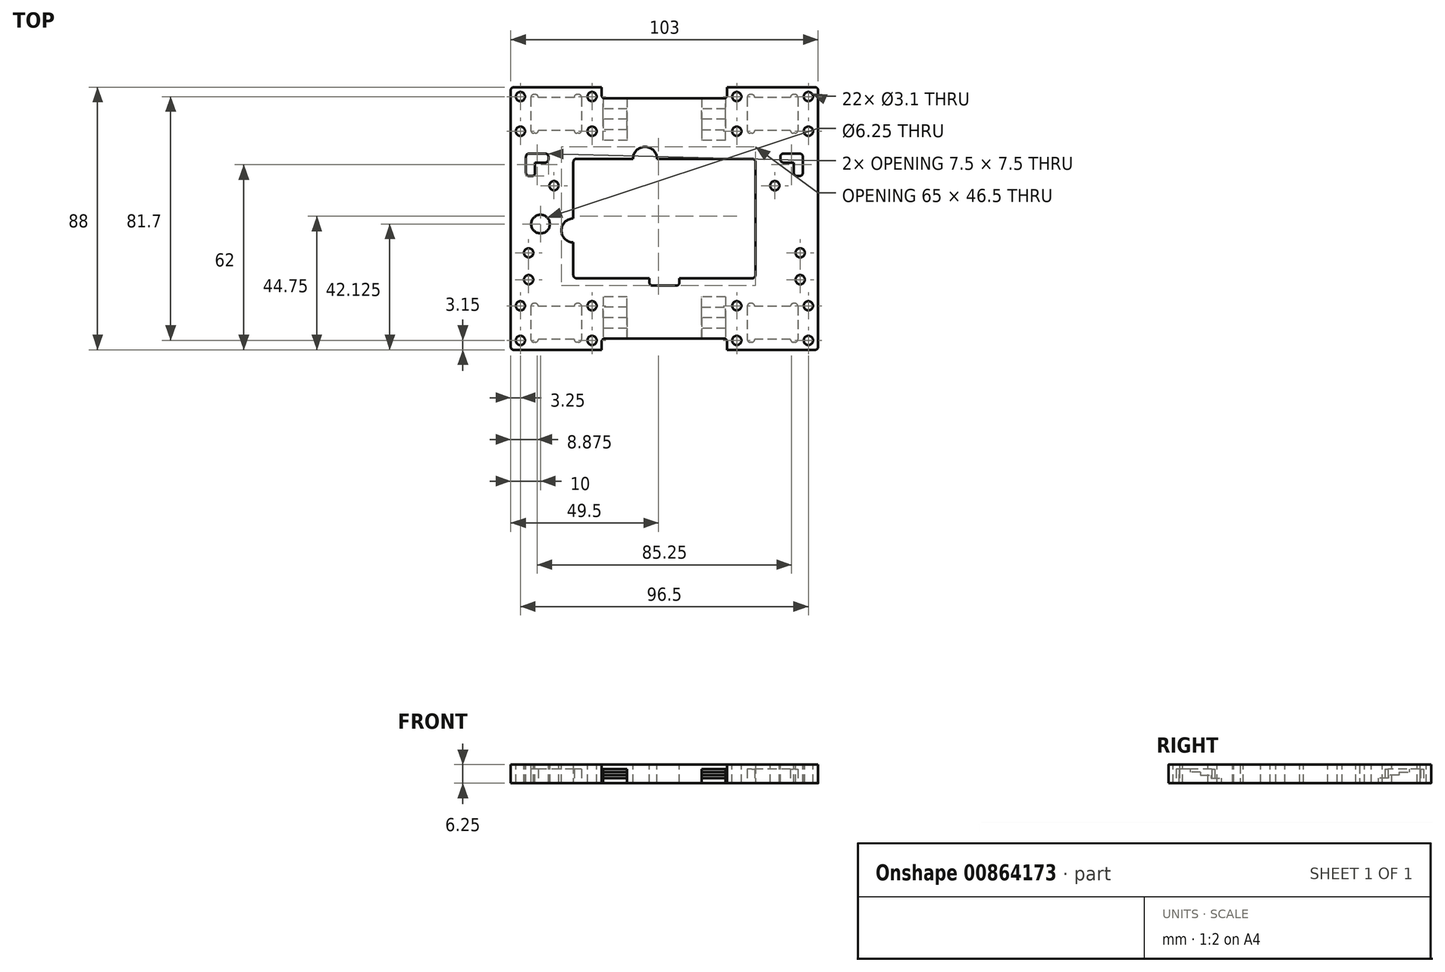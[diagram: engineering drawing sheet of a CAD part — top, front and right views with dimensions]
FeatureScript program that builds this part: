
annotation { "Feature Type Name" : "Feature", "Feature Type Description" : "" }
export const myFeature = defineFeature(function(context is Context, id is Id, definition is map)
    precondition{}
    {
        {
            var Q0;
            Q0=qCreatedBy(makeId("Top.planeOp"),FACE);
            var sketch = newSketch(context, id + "F0", { "sketchPlane" : qUnion([Q0])});
            skLineSegment(sketch, "E0.bottom", {"start": v(51.5, 44) * mm, "end": v(-51.5, 44) * mm, "construction": true});
            skLineSegment(sketch, "E0.top", {"start": v(51.5, -44) * mm, "end": v(-51.5, -44) * mm, "construction": true});
            skLineSegment(sketch, "E0.left", {"start": v(51.5, 44) * mm, "end": v(51.5, -44) * mm});
            skLineSegment(sketch, "E0.right", {"start": v(-51.5, 44) * mm, "end": v(-51.5, -44) * mm});
            skPoint(sketch, "E0.middle", {"position": v(0, 0) * mm});
            skLineSegment(sketch, "E1", {"start": v(-51.5, 44) * mm, "end": v(-21, 44) * mm, "construction": true});
            skLineSegment(sketch, "E2", {"start": v(-21, 44) * mm, "end": v(-21, 40.25) * mm});
            skLineSegment(sketch, "E3", {"start": v(-21, 40.25) * mm, "end": v(21, 40.25) * mm});
            skLineSegment(sketch, "E4", {"start": v(21, 40.25) * mm, "end": v(21, 44) * mm});
            skLineSegment(sketch, "E5", {"start": v(21, 44) * mm, "end": v(51.5, 44) * mm, "construction": true});
            skLineSegment(sketch, "E6", {"start": v(51.5, -44) * mm, "end": v(21, -44) * mm, "construction": true});
            skLineSegment(sketch, "E7", {"start": v(21, -44) * mm, "end": v(21, -40.25) * mm});
            skLineSegment(sketch, "E8", {"start": v(21, -40.25) * mm, "end": v(-21, -40.25) * mm});
            skLineSegment(sketch, "E9", {"start": v(-21, -40.25) * mm, "end": v(-21, -44) * mm});
            skLineSegment(sketch, "E10", {"start": v(-21, -44) * mm, "end": v(-51.5, -44) * mm, "construction": true});
            skLineSegment(sketch, "E11", {"start": v(0, 40.25) * mm, "end": v(0, 0) * mm, "construction": true});
            skLineSegment(sketch, "E12", {"start": v(0, -40.25) * mm, "end": v(0, 0) * mm, "construction": true});
            skLineSegment(sketch, "E13", {"start": v(-51.5, 44) * mm, "end": v(-21, 44) * mm});
            skLineSegment(sketch, "E14", {"start": v(21, 44) * mm, "end": v(51.5, 44) * mm});
            skLineSegment(sketch, "E15", {"start": v(51.5, -44) * mm, "end": v(21, -44) * mm});
            skLineSegment(sketch, "E16", {"start": v(-21, -44) * mm, "end": v(-51.5, -44) * mm});
            skLineSegment(sketch, "E17.bottom", {"start": v(30.5, 20) * mm, "end": v(-30.5, 20) * mm});
            skLineSegment(sketch, "E17.top", {"start": v(30.5, -20) * mm, "end": v(-30.5, -20) * mm});
            skLineSegment(sketch, "E17.left", {"start": v(30.5, 20) * mm, "end": v(30.5, -20) * mm});
            skLineSegment(sketch, "E17.right", {"start": v(-30.5, 20) * mm, "end": v(-30.5, -20) * mm});
            skSolve(sketch);
        }
        {
            var Q0;
            Q0=makeQuery(id+"F0.imprint","IMPRINT",FACE,{"disambiguationData":[TD([[makeQuery(id+"F0.imprint","IMPRINT",EDGE,{"derivedFrom":sQuery(id+"F0.wireOp",EDGE,"E0.left")}),-1.0]])]});
            extrude(context, id + "F1", {"entities" : qUnion([Q0]), "depth" : 6.25 * mm, "offsetDistance" : 25 * mm});
        }
        {
            var Q0;
            Q0=makeQuery(id+"F1.opExtrude","CAP_FACE",FACE,{"disambiguationData":[OSD([sQuery(id+"F0.wireOp",EDGE,"E0.left"),sQuery(id+"F0.wireOp",EDGE,"E0.right"),sQuery(id+"F0.wireOp",EDGE,"E2"),sQuery(id+"F0.wireOp",EDGE,"E3"),sQuery(id+"F0.wireOp",EDGE,"E4"),sQuery(id+"F0.wireOp",EDGE,"E7"),sQuery(id+"F0.wireOp",EDGE,"E8"),sQuery(id+"F0.wireOp",EDGE,"E9"),sQuery(id+"F0.wireOp",EDGE,"E13"),sQuery(id+"F0.wireOp",EDGE,"E14"),sQuery(id+"F0.wireOp",EDGE,"E15"),sQuery(id+"F0.wireOp",EDGE,"E16"),sQuery(id+"F0.wireOp",EDGE,"E17.bottom"),sQuery(id+"F0.wireOp",EDGE,"E17.top"),sQuery(id+"F0.wireOp",EDGE,"E17.left"),sQuery(id+"F0.wireOp",EDGE,"E17.right")])],"isStart":false});
            var sketch = newSketch(context, id + "F2", { "sketchPlane" : qUnion([Q0])});
            skLineSegment(sketch, "E18.bottom", {"start": v(-48.25, 40.85) * mm, "end": v(-24.25, 40.85) * mm, "construction": true});
            skLineSegment(sketch, "E18.top", {"start": v(-48.25, 29.25) * mm, "end": v(-24.25, 29.25) * mm, "construction": true});
            skLineSegment(sketch, "E18.left", {"start": v(-48.25, 40.85) * mm, "end": v(-48.25, 29.25) * mm, "construction": true});
            skLineSegment(sketch, "E18.right", {"start": v(-24.25, 40.85) * mm, "end": v(-24.25, 29.25) * mm, "construction": true});
            skLineSegment(sketch, "E19.bottom", {"start": v(24.25, 40.85) * mm, "end": v(48.25, 40.85) * mm, "construction": true});
            skLineSegment(sketch, "E19.top", {"start": v(24.25, 29.25) * mm, "end": v(48.25, 29.25) * mm, "construction": true});
            skLineSegment(sketch, "E19.left", {"start": v(24.25, 40.85) * mm, "end": v(24.25, 29.25) * mm, "construction": true});
            skLineSegment(sketch, "E19.right", {"start": v(48.25, 40.85) * mm, "end": v(48.25, 29.25) * mm, "construction": true});
            skLineSegment(sketch, "E20.bottom", {"start": v(24.25, -29.25) * mm, "end": v(48.25, -29.25) * mm, "construction": true});
            skLineSegment(sketch, "E20.top", {"start": v(24.25, -40.85) * mm, "end": v(48.25, -40.85) * mm, "construction": true});
            skLineSegment(sketch, "E20.left", {"start": v(24.25, -29.25) * mm, "end": v(24.25, -40.85) * mm, "construction": true});
            skLineSegment(sketch, "E20.right", {"start": v(48.25, -29.25) * mm, "end": v(48.25, -40.85) * mm, "construction": true});
            skLineSegment(sketch, "E21.bottom", {"start": v(-48.25, -29.25) * mm, "end": v(-24.25, -29.25) * mm, "construction": true});
            skLineSegment(sketch, "E21.top", {"start": v(-48.25, -40.85) * mm, "end": v(-24.25, -40.85) * mm, "construction": true});
            skLineSegment(sketch, "E21.left", {"start": v(-48.25, -29.25) * mm, "end": v(-48.25, -40.85) * mm, "construction": true});
            skLineSegment(sketch, "E21.right", {"start": v(-24.25, -29.25) * mm, "end": v(-24.25, -40.85) * mm, "construction": true});
            skLineSegment(sketch, "E22", {"start": v(-24.25, 29.25) * mm, "end": v(24.25, 29.25) * mm, "construction": true});
            skLineSegment(sketch, "E23", {"start": v(24.25, -29.25) * mm, "end": v(-24.25, -29.25) * mm, "construction": true});
            skLineSegment(sketch, "E24", {"start": v(0, 29.25) * mm, "end": v(0, 0) * mm, "construction": true});
            skLineSegment(sketch, "E25", {"start": v(0, 0) * mm, "end": v(0, -29.25) * mm, "construction": true});
            skCircle(sketch, "E26", {"center": v(-48.25, 40.85) * mm, "radius": 1.55 * mm});
            skCircle(sketch, "E27", {"center": v(-24.25, 40.85) * mm, "radius": 1.55 * mm});
            skCircle(sketch, "E28", {"center": v(-24.25, 29.25) * mm, "radius": 1.55 * mm});
            skCircle(sketch, "E29", {"center": v(-48.25, 29.25) * mm, "radius": 1.55 * mm});
            skCircle(sketch, "E30", {"center": v(24.25, 40.85) * mm, "radius": 1.55 * mm});
            skCircle(sketch, "E31", {"center": v(48.25, 40.85) * mm, "radius": 1.55 * mm});
            skCircle(sketch, "E32", {"center": v(48.25, 29.25) * mm, "radius": 1.55 * mm});
            skCircle(sketch, "E33", {"center": v(24.25, 29.25) * mm, "radius": 1.55 * mm});
            skCircle(sketch, "E34", {"center": v(24.25, -29.25) * mm, "radius": 1.55 * mm});
            skCircle(sketch, "E35", {"center": v(24.25, -40.85) * mm, "radius": 1.55 * mm});
            skCircle(sketch, "E36", {"center": v(48.25, -29.25) * mm, "radius": 1.55 * mm});
            skCircle(sketch, "E37", {"center": v(48.25, -40.85) * mm, "radius": 1.55 * mm});
            skCircle(sketch, "E38", {"center": v(-24.25, -29.25) * mm, "radius": 1.55 * mm});
            skCircle(sketch, "E39", {"center": v(-48.25, -29.25) * mm, "radius": 1.55 * mm});
            skCircle(sketch, "E40", {"center": v(-48.25, -40.85) * mm, "radius": 1.55 * mm});
            skCircle(sketch, "E41", {"center": v(-24.25, -40.85) * mm, "radius": 1.55 * mm});
            skLineSegment(sketch, "E42", {"start": v(-46.38, 21.75) * mm, "end": v(-38.88, 21.75) * mm});
            skLineSegment(sketch, "E43", {"start": v(-38.88, 21.75) * mm, "end": v(-38.88, 18.75) * mm});
            skLineSegment(sketch, "E44", {"start": v(-38.88, 18.75) * mm, "end": v(-43.38, 18.75) * mm});
            skLineSegment(sketch, "E45", {"start": v(-43.38, 18.75) * mm, "end": v(-43.38, 14.25) * mm});
            skLineSegment(sketch, "E46", {"start": v(-43.38, 14.25) * mm, "end": v(-46.38, 14.25) * mm});
            skLineSegment(sketch, "E47", {"start": v(-46.38, 14.25) * mm, "end": v(-46.38, 21.75) * mm});
            skLineSegment(sketch, "E48", {"start": v(38.88, 21.75) * mm, "end": v(46.38, 21.75) * mm});
            skLineSegment(sketch, "E49", {"start": v(46.38, 21.75) * mm, "end": v(46.38, 14.25) * mm});
            skLineSegment(sketch, "E50", {"start": v(46.38, 14.25) * mm, "end": v(43.38, 14.25) * mm});
            skLineSegment(sketch, "E51", {"start": v(43.38, 14.25) * mm, "end": v(43.38, 18.75) * mm});
            skLineSegment(sketch, "E52", {"start": v(43.38, 18.75) * mm, "end": v(38.88, 18.75) * mm});
            skLineSegment(sketch, "E53", {"start": v(38.88, 18.75) * mm, "end": v(38.88, 21.75) * mm});
            skLineSegment(sketch, "E54", {"start": v(-38.88, 21.75) * mm, "end": v(38.88, 21.75) * mm, "construction": true});
            skLineSegment(sketch, "E55", {"start": v(0, 21.75) * mm, "end": v(0, 0) * mm});
            skLineSegment(sketch, "E56", {"start": v(-37, 11) * mm, "end": v(37, 11) * mm, "construction": true});
            skLineSegment(sketch, "E57", {"start": v(0, 11) * mm, "end": v(0, 0) * mm});
            skCircle(sketch, "E58", {"center": v(-37, 11) * mm, "radius": 1.55 * mm});
            skCircle(sketch, "E59", {"center": v(37, 11) * mm, "radius": 1.55 * mm});
            skLineSegment(sketch, "E60.bottom", {"start": v(45.5, -11.5) * mm, "end": v(-45.5, -11.5) * mm, "construction": true});
            skLineSegment(sketch, "E60.top", {"start": v(45.5, -20.5) * mm, "end": v(-45.5, -20.5) * mm, "construction": true});
            skLineSegment(sketch, "E60.left", {"start": v(45.5, -11.5) * mm, "end": v(45.5, -20.5) * mm, "construction": true});
            skLineSegment(sketch, "E60.right", {"start": v(-45.5, -11.5) * mm, "end": v(-45.5, -20.5) * mm, "construction": true});
            skPoint(sketch, "E60.middle", {"position": v(0, -16) * mm});
            skCircle(sketch, "E61", {"center": v(-45.5, -11.5) * mm, "radius": 1.55 * mm});
            skCircle(sketch, "E62", {"center": v(-45.5, -20.5) * mm, "radius": 1.55 * mm});
            skCircle(sketch, "E63", {"center": v(45.5, -11.5) * mm, "radius": 1.55 * mm});
            skCircle(sketch, "E64", {"center": v(45.5, -20.5) * mm, "radius": 1.55 * mm});
            skCircle(sketch, "E65", {"center": v(-41.5, -1.87) * mm, "radius": 3.12 * mm});
            skSolve(sketch);
        }
        {
            var Q0;
            Q0 = qSketchRegion(id + "F2", true);
            extrude(context, id + "F3", {"entities" : qUnion([Q0]), "operationType" : NewBodyOperationType.REMOVE, "oppositeDirection" : true, "depth" : 25 * mm, "offsetDistance" : 25 * mm});
        }
        {
            var Q0;
            Q0=makeQuery(id+"F1.opExtrude","CAP_FACE",FACE,{"disambiguationData":[OSD([sQuery(id+"F0.wireOp",EDGE,"E0.left"),sQuery(id+"F0.wireOp",EDGE,"E0.right"),sQuery(id+"F0.wireOp",EDGE,"E2"),sQuery(id+"F0.wireOp",EDGE,"E3"),sQuery(id+"F0.wireOp",EDGE,"E4"),sQuery(id+"F0.wireOp",EDGE,"E7"),sQuery(id+"F0.wireOp",EDGE,"E8"),sQuery(id+"F0.wireOp",EDGE,"E9"),sQuery(id+"F0.wireOp",EDGE,"E13"),sQuery(id+"F0.wireOp",EDGE,"E14"),sQuery(id+"F0.wireOp",EDGE,"E15"),sQuery(id+"F0.wireOp",EDGE,"E16"),sQuery(id+"F0.wireOp",EDGE,"E17.bottom"),sQuery(id+"F0.wireOp",EDGE,"E17.top"),sQuery(id+"F0.wireOp",EDGE,"E17.left"),sQuery(id+"F0.wireOp",EDGE,"E17.right")])],"isStart":false});
            var sketch = newSketch(context, id + "F4", { "sketchPlane" : qUnion([Q0])});
            skCircle(sketch, "E66", {"center": v(-6.5, 20) * mm, "radius": 4 * mm});
            skCircle(sketch, "E67", {"center": v(-30.5, -4) * mm, "radius": 4 * mm});
            skLineSegment(sketch, "E68.bottom", {"start": v(-5, -20) * mm, "end": v(5, -20) * mm});
            skLineSegment(sketch, "E68.top", {"start": v(-5, -22.5) * mm, "end": v(5, -22.5) * mm});
            skLineSegment(sketch, "E68.left", {"start": v(-5, -20) * mm, "end": v(-5, -22.5) * mm});
            skLineSegment(sketch, "E68.right", {"start": v(5, -20) * mm, "end": v(5, -22.5) * mm});
            skLineSegment(sketch, "E69", {"start": v(0, 0) * mm, "end": v(0, -20) * mm, "construction": true});
            skSolve(sketch);
        }
        {
            var Q0;
            Q0 = qSketchRegion(id + "F4", true);
            extrude(context, id + "F5", {"entities" : qUnion([Q0]), "operationType" : NewBodyOperationType.REMOVE, "oppositeDirection" : true, "depth" : 25 * mm, "offsetDistance" : 25 * mm});
        }
        {
            var Q0;
            Q0=makeQuery(id+"F1.opExtrude","SWEPT_EDGE",EDGE,{"disambiguationData":[OSD([sQuery(id+"F0.wireOp",EDGE,"E0.left"),sQuery(id+"F0.wireOp",EDGE,"E14")])]});
            var Q1;
            Q1=makeQuery(id+"F1.opExtrude","SWEPT_EDGE",EDGE,{"disambiguationData":[OSD([sQuery(id+"F0.wireOp",EDGE,"E2"),sQuery(id+"F0.wireOp",EDGE,"E3")])]});
            var Q2;
            Q2=makeQuery(id+"F1.opExtrude","SWEPT_EDGE",EDGE,{"disambiguationData":[OSD([sQuery(id+"F0.wireOp",EDGE,"E3"),sQuery(id+"F0.wireOp",EDGE,"E4")])]});
            var Q3;
            Q3=makeQuery(id+"F1.opExtrude","SWEPT_EDGE",EDGE,{"disambiguationData":[OSD([sQuery(id+"F0.wireOp",EDGE,"E0.right"),sQuery(id+"F0.wireOp",EDGE,"E13")])]});
            var Q4;
            Q4=makeQuery(id+"F3.boolean.opBoolean","COPY",EDGE,{"derivedFrom":makeQuery(id+"F3.opExtrude","SWEPT_EDGE",EDGE,{"disambiguationData":[OSD([sQuery(id+"F2.wireOp",EDGE,"E49"),sQuery(id+"F2.wireOp",EDGE,"E50")])]})});
            var Q5;
            Q5=makeQuery(id+"F3.boolean.opBoolean","COPY",EDGE,{"derivedFrom":makeQuery(id+"F3.opExtrude","SWEPT_EDGE",EDGE,{"disambiguationData":[OSD([sQuery(id+"F2.wireOp",EDGE,"E50"),sQuery(id+"F2.wireOp",EDGE,"E51")])]})});
            var Q6;
            Q6=makeQuery(id+"F3.boolean.opBoolean","COPY",EDGE,{"derivedFrom":makeQuery(id+"F3.opExtrude","SWEPT_EDGE",EDGE,{"disambiguationData":[OSD([sQuery(id+"F2.wireOp",EDGE,"E52"),sQuery(id+"F2.wireOp",EDGE,"E53")])]})});
            var Q7;
            Q7=makeQuery(id+"F3.boolean.opBoolean","COPY",EDGE,{"derivedFrom":makeQuery(id+"F3.opExtrude","SWEPT_EDGE",EDGE,{"disambiguationData":[OSD([sQuery(id+"F2.wireOp",EDGE,"E48"),sQuery(id+"F2.wireOp",EDGE,"E53")])]})});
            var Q8;
            Q8=makeQuery(id+"F3.boolean.opBoolean","COPY",EDGE,{"derivedFrom":makeQuery(id+"F3.opExtrude","SWEPT_EDGE",EDGE,{"disambiguationData":[OSD([sQuery(id+"F2.wireOp",EDGE,"E48"),sQuery(id+"F2.wireOp",EDGE,"E49")])]})});
            var Q9;
            Q9=makeQuery(id+"F1.opExtrude","SWEPT_EDGE",EDGE,{"disambiguationData":[OSD([sQuery(id+"F0.wireOp",EDGE,"E17.bottom"),sQuery(id+"F0.wireOp",EDGE,"E17.left")])]});
            var Q10;
            Q10=makeQuery(id+"F1.opExtrude","SWEPT_EDGE",EDGE,{"disambiguationData":[OSD([sQuery(id+"F0.wireOp",EDGE,"E17.bottom"),sQuery(id+"F0.wireOp",EDGE,"E17.right")])]});
            var Q11;
            Q11=makeQuery(id+"F3.boolean.opBoolean","COPY",EDGE,{"derivedFrom":makeQuery(id+"F3.opExtrude","SWEPT_EDGE",EDGE,{"disambiguationData":[OSD([sQuery(id+"F2.wireOp",EDGE,"E42"),sQuery(id+"F2.wireOp",EDGE,"E47")])]})});
            var Q12;
            Q12=makeQuery(id+"F3.boolean.opBoolean","COPY",EDGE,{"derivedFrom":makeQuery(id+"F3.opExtrude","SWEPT_EDGE",EDGE,{"disambiguationData":[OSD([sQuery(id+"F2.wireOp",EDGE,"E42"),sQuery(id+"F2.wireOp",EDGE,"E43")])]})});
            var Q13;
            Q13=makeQuery(id+"F3.boolean.opBoolean","COPY",EDGE,{"derivedFrom":makeQuery(id+"F3.opExtrude","SWEPT_EDGE",EDGE,{"disambiguationData":[OSD([sQuery(id+"F2.wireOp",EDGE,"E43"),sQuery(id+"F2.wireOp",EDGE,"E44")])]})});
            var Q14;
            Q14=makeQuery(id+"F3.boolean.opBoolean","COPY",EDGE,{"derivedFrom":makeQuery(id+"F3.opExtrude","SWEPT_EDGE",EDGE,{"disambiguationData":[OSD([sQuery(id+"F2.wireOp",EDGE,"E45"),sQuery(id+"F2.wireOp",EDGE,"E46")])]})});
            var Q15;
            Q15=makeQuery(id+"F3.boolean.opBoolean","COPY",EDGE,{"derivedFrom":makeQuery(id+"F3.opExtrude","SWEPT_EDGE",EDGE,{"disambiguationData":[OSD([sQuery(id+"F2.wireOp",EDGE,"E46"),sQuery(id+"F2.wireOp",EDGE,"E47")])]})});
            var Q16;
            Q16=makeQuery(id+"F1.opExtrude","SWEPT_EDGE",EDGE,{"disambiguationData":[OSD([sQuery(id+"F0.wireOp",EDGE,"E0.right"),sQuery(id+"F0.wireOp",EDGE,"E16")])]});
            var Q17;
            Q17=makeQuery(id+"F1.opExtrude","SWEPT_EDGE",EDGE,{"disambiguationData":[OSD([sQuery(id+"F0.wireOp",EDGE,"E7"),sQuery(id+"F0.wireOp",EDGE,"E8")])]});
            var Q18;
            Q18=makeQuery(id+"F1.opExtrude","SWEPT_EDGE",EDGE,{"disambiguationData":[OSD([sQuery(id+"F0.wireOp",EDGE,"E0.left"),sQuery(id+"F0.wireOp",EDGE,"E15")])]});
            var Q19;
            Q19=makeQuery(id+"F1.opExtrude","SWEPT_EDGE",EDGE,{"disambiguationData":[OSD([sQuery(id+"F0.wireOp",EDGE,"E8"),sQuery(id+"F0.wireOp",EDGE,"E9")])]});
            var Q20;
            Q20=makeQuery(id+"F1.opExtrude","SWEPT_EDGE",EDGE,{"disambiguationData":[OSD([sQuery(id+"F0.wireOp",EDGE,"E17.top"),sQuery(id+"F0.wireOp",EDGE,"E17.right")])]});
            var Q21;
            Q21=makeQuery(id+"F5.boolean.opBoolean","COPY",EDGE,{"derivedFrom":makeQuery(id+"F5.opExtrude","SWEPT_EDGE",EDGE,{"disambiguationData":[OSD([sQuery(id+"F4.wireOp",EDGE,"E68.top"),sQuery(id+"F4.wireOp",EDGE,"E68.left")])]})});
            var Q22;
            Q22=makeQuery(id+"F1.opExtrude","SWEPT_EDGE",EDGE,{"disambiguationData":[OSD([sQuery(id+"F0.wireOp",EDGE,"E17.top"),sQuery(id+"F0.wireOp",EDGE,"E17.left")])]});
            var Q23;
            Q23=makeQuery(id+"F5.boolean.opBoolean","COPY",EDGE,{"derivedFrom":makeQuery(id+"F5.opExtrude","SWEPT_EDGE",EDGE,{"disambiguationData":[OSD([sQuery(id+"F4.wireOp",EDGE,"E68.top"),sQuery(id+"F4.wireOp",EDGE,"E68.right")])]})});
            fillet(context, id + "F6", {"entities" : qUnion([Q0, Q1, Q2, Q3, Q4, Q5, Q6, Q7, Q8, Q9, Q10, Q11, Q12, Q13, Q14, Q15, Q16, Q17, Q18, Q19, Q20, Q21, Q22, Q23]), "radius" : 1 * mm, "tangentPropagation" : true, "allowEdgeOverflow" : false});
        }
        {
            var Q0;
            Q0=makeQuery(id+"F1.opExtrude","CAP_FACE",FACE,{"disambiguationData":[OSD([sQuery(id+"F0.wireOp",EDGE,"E0.left"),sQuery(id+"F0.wireOp",EDGE,"E0.right"),sQuery(id+"F0.wireOp",EDGE,"E2"),sQuery(id+"F0.wireOp",EDGE,"E3"),sQuery(id+"F0.wireOp",EDGE,"E4"),sQuery(id+"F0.wireOp",EDGE,"E7"),sQuery(id+"F0.wireOp",EDGE,"E8"),sQuery(id+"F0.wireOp",EDGE,"E9"),sQuery(id+"F0.wireOp",EDGE,"E13"),sQuery(id+"F0.wireOp",EDGE,"E14"),sQuery(id+"F0.wireOp",EDGE,"E15"),sQuery(id+"F0.wireOp",EDGE,"E16"),sQuery(id+"F0.wireOp",EDGE,"E17.bottom"),sQuery(id+"F0.wireOp",EDGE,"E17.top"),sQuery(id+"F0.wireOp",EDGE,"E17.left"),sQuery(id+"F0.wireOp",EDGE,"E17.right")])],"isStart":true});
            var sketch = newSketch(context, id + "F7", { "sketchPlane" : qUnion([Q0])});
            skLineSegment(sketch, "E70", {"start": v(48.25, -40.85) * mm, "end": v(24.25, -29.25) * mm, "construction": true});
            skLineSegment(sketch, "E71.bottom", {"start": v(27.75, -41.55) * mm, "end": v(44.75, -41.55) * mm, "construction": true});
            skLineSegment(sketch, "E71.top", {"start": v(27.75, -28.55) * mm, "end": v(44.75, -28.55) * mm, "construction": true});
            skLineSegment(sketch, "E71.left", {"start": v(27.75, -41.55) * mm, "end": v(27.75, -28.55) * mm});
            skLineSegment(sketch, "E71.right", {"start": v(44.75, -41.55) * mm, "end": v(44.75, -28.55) * mm});
            skPoint(sketch, "E71.middle", {"position": v(36.25, -35.05) * mm});
            skLineSegment(sketch, "E72", {"start": v(44.75, -41.55) * mm, "end": v(42.25, -41.55) * mm});
            skLineSegment(sketch, "E73", {"start": v(42.25, -41.55) * mm, "end": v(42.25, -40.55) * mm});
            skLineSegment(sketch, "E74", {"start": v(42.25, -40.55) * mm, "end": v(30.25, -40.55) * mm});
            skLineSegment(sketch, "E75", {"start": v(30.25, -40.55) * mm, "end": v(30.25, -41.55) * mm});
            skLineSegment(sketch, "E76", {"start": v(30.25, -41.55) * mm, "end": v(27.75, -41.55) * mm});
            skLineSegment(sketch, "E77", {"start": v(44.75, -28.55) * mm, "end": v(42.25, -28.55) * mm});
            skLineSegment(sketch, "E78", {"start": v(42.25, -28.55) * mm, "end": v(42.25, -29.55) * mm});
            skLineSegment(sketch, "E79", {"start": v(42.25, -29.55) * mm, "end": v(30.25, -29.55) * mm});
            skLineSegment(sketch, "E80", {"start": v(30.25, -29.55) * mm, "end": v(30.25, -28.55) * mm});
            skLineSegment(sketch, "E81", {"start": v(30.25, -28.55) * mm, "end": v(27.75, -28.55) * mm});
            skLineSegment(sketch, "E82.0.1.0", {"start": v(48.25, 29.15) * mm, "end": v(24.25, 40.75) * mm, "construction": true});
            skLineSegment(sketch, "E82.0.1.1", {"start": v(27.75, 28.45) * mm, "end": v(44.75, 28.45) * mm, "construction": true});
            skPoint(sketch, "E82.0.1.2", {"position": v(36.25, 34.95) * mm});
            skLineSegment(sketch, "E82.0.1.3", {"start": v(27.75, 41.45) * mm, "end": v(44.75, 41.45) * mm, "construction": true});
            skLineSegment(sketch, "E82.0.1.4", {"start": v(42.25, 29.45) * mm, "end": v(30.25, 29.45) * mm});
            skLineSegment(sketch, "E82.0.1.5", {"start": v(44.75, 28.45) * mm, "end": v(44.75, 41.45) * mm});
            skLineSegment(sketch, "E82.0.1.6", {"start": v(42.25, 40.45) * mm, "end": v(30.25, 40.45) * mm});
            skLineSegment(sketch, "E82.0.1.7", {"start": v(27.75, 28.45) * mm, "end": v(27.75, 41.45) * mm});
            skLineSegment(sketch, "E82.0.1.8", {"start": v(42.25, 41.45) * mm, "end": v(42.25, 40.45) * mm});
            skLineSegment(sketch, "E82.0.1.9", {"start": v(30.25, 40.45) * mm, "end": v(30.25, 41.45) * mm});
            skLineSegment(sketch, "E82.0.1.10", {"start": v(30.25, 28.45) * mm, "end": v(27.75, 28.45) * mm});
            skLineSegment(sketch, "E82.0.1.11", {"start": v(44.75, 28.45) * mm, "end": v(42.25, 28.45) * mm});
            skLineSegment(sketch, "E82.0.1.12", {"start": v(30.25, 41.45) * mm, "end": v(27.75, 41.45) * mm});
            skLineSegment(sketch, "E82.0.1.13", {"start": v(42.25, 28.45) * mm, "end": v(42.25, 29.45) * mm});
            skLineSegment(sketch, "E82.0.1.14", {"start": v(30.25, 29.45) * mm, "end": v(30.25, 28.45) * mm});
            skLineSegment(sketch, "E82.0.1.15", {"start": v(44.75, 41.45) * mm, "end": v(42.25, 41.45) * mm});
            skLineSegment(sketch, "E82.1.0.0", {"start": v(-24.25, -40.85) * mm, "end": v(-48.25, -29.25) * mm, "construction": true});
            skLineSegment(sketch, "E82.1.0.1", {"start": v(-44.75, -41.55) * mm, "end": v(-27.75, -41.55) * mm, "construction": true});
            skPoint(sketch, "E82.1.0.2", {"position": v(-36.25, -35.05) * mm});
            skLineSegment(sketch, "E82.1.0.3", {"start": v(-44.75, -28.55) * mm, "end": v(-27.75, -28.55) * mm, "construction": true});
            skLineSegment(sketch, "E82.1.0.4", {"start": v(-30.25, -40.55) * mm, "end": v(-42.25, -40.55) * mm});
            skLineSegment(sketch, "E82.1.0.5", {"start": v(-27.75, -41.55) * mm, "end": v(-27.75, -28.55) * mm});
            skLineSegment(sketch, "E82.1.0.6", {"start": v(-30.25, -29.55) * mm, "end": v(-42.25, -29.55) * mm});
            skLineSegment(sketch, "E82.1.0.7", {"start": v(-44.75, -41.55) * mm, "end": v(-44.75, -28.55) * mm});
            skLineSegment(sketch, "E82.1.0.8", {"start": v(-30.25, -28.55) * mm, "end": v(-30.25, -29.55) * mm});
            skLineSegment(sketch, "E82.1.0.9", {"start": v(-42.25, -29.55) * mm, "end": v(-42.25, -28.55) * mm});
            skLineSegment(sketch, "E82.1.0.10", {"start": v(-42.25, -41.55) * mm, "end": v(-44.75, -41.55) * mm});
            skLineSegment(sketch, "E82.1.0.11", {"start": v(-27.75, -41.55) * mm, "end": v(-30.25, -41.55) * mm});
            skLineSegment(sketch, "E82.1.0.12", {"start": v(-42.25, -28.55) * mm, "end": v(-44.75, -28.55) * mm});
            skLineSegment(sketch, "E82.1.0.13", {"start": v(-30.25, -41.55) * mm, "end": v(-30.25, -40.55) * mm});
            skLineSegment(sketch, "E82.1.0.14", {"start": v(-42.25, -40.55) * mm, "end": v(-42.25, -41.55) * mm});
            skLineSegment(sketch, "E82.1.0.15", {"start": v(-27.75, -28.55) * mm, "end": v(-30.25, -28.55) * mm});
            skLineSegment(sketch, "E82.1.1.0", {"start": v(-24.25, 29.15) * mm, "end": v(-48.25, 40.75) * mm, "construction": true});
            skLineSegment(sketch, "E82.1.1.1", {"start": v(-44.75, 28.45) * mm, "end": v(-27.75, 28.45) * mm, "construction": true});
            skPoint(sketch, "E82.1.1.2", {"position": v(-36.25, 34.95) * mm});
            skLineSegment(sketch, "E82.1.1.3", {"start": v(-44.75, 41.45) * mm, "end": v(-27.75, 41.45) * mm, "construction": true});
            skLineSegment(sketch, "E82.1.1.4", {"start": v(-30.25, 29.45) * mm, "end": v(-42.25, 29.45) * mm});
            skLineSegment(sketch, "E82.1.1.5", {"start": v(-27.75, 28.45) * mm, "end": v(-27.75, 41.45) * mm});
            skLineSegment(sketch, "E82.1.1.6", {"start": v(-30.25, 40.45) * mm, "end": v(-42.25, 40.45) * mm});
            skLineSegment(sketch, "E82.1.1.7", {"start": v(-44.75, 28.45) * mm, "end": v(-44.75, 41.45) * mm});
            skLineSegment(sketch, "E82.1.1.8", {"start": v(-30.25, 41.45) * mm, "end": v(-30.25, 40.45) * mm});
            skLineSegment(sketch, "E82.1.1.9", {"start": v(-42.25, 40.45) * mm, "end": v(-42.25, 41.45) * mm});
            skLineSegment(sketch, "E82.1.1.10", {"start": v(-42.25, 28.45) * mm, "end": v(-44.75, 28.45) * mm});
            skLineSegment(sketch, "E82.1.1.11", {"start": v(-27.75, 28.45) * mm, "end": v(-30.25, 28.45) * mm});
            skLineSegment(sketch, "E82.1.1.12", {"start": v(-42.25, 41.45) * mm, "end": v(-44.75, 41.45) * mm});
            skLineSegment(sketch, "E82.1.1.13", {"start": v(-30.25, 28.45) * mm, "end": v(-30.25, 29.45) * mm});
            skLineSegment(sketch, "E82.1.1.14", {"start": v(-42.25, 29.45) * mm, "end": v(-42.25, 28.45) * mm});
            skLineSegment(sketch, "E82.1.1.15", {"start": v(-27.75, 41.45) * mm, "end": v(-30.25, 41.45) * mm});
            skLineSegment(sketch, "E82.direction1", {"start": v(27.75, -41.55) * mm, "end": v(-44.75, -41.55) * mm, "construction": true});
            skLineSegment(sketch, "E82.direction2", {"start": v(27.75, -41.55) * mm, "end": v(27.75, 28.45) * mm, "construction": true});
            skSolve(sketch);
        }
        {
            var Q0;
            Q0 = qSketchRegion(id + "F7", true);
            extrude(context, id + "F8", {"entities" : qUnion([Q0]), "operationType" : NewBodyOperationType.REMOVE, "oppositeDirection" : true, "depth" : 4.75 * mm, "offsetDistance" : 25 * mm});
        }
        {
            var Q0;
            Q0=makeQuery(id+"F1.opExtrude","CAP_FACE",FACE,{"disambiguationData":[OSD([sQuery(id+"F0.wireOp",EDGE,"E0.left"),sQuery(id+"F0.wireOp",EDGE,"E0.right"),sQuery(id+"F0.wireOp",EDGE,"E2"),sQuery(id+"F0.wireOp",EDGE,"E3"),sQuery(id+"F0.wireOp",EDGE,"E4"),sQuery(id+"F0.wireOp",EDGE,"E7"),sQuery(id+"F0.wireOp",EDGE,"E8"),sQuery(id+"F0.wireOp",EDGE,"E9"),sQuery(id+"F0.wireOp",EDGE,"E13"),sQuery(id+"F0.wireOp",EDGE,"E14"),sQuery(id+"F0.wireOp",EDGE,"E15"),sQuery(id+"F0.wireOp",EDGE,"E16"),sQuery(id+"F0.wireOp",EDGE,"E17.bottom"),sQuery(id+"F0.wireOp",EDGE,"E17.top"),sQuery(id+"F0.wireOp",EDGE,"E17.left"),sQuery(id+"F0.wireOp",EDGE,"E17.right")])],"isStart":true});
            var sketch = newSketch(context, id + "F9", { "sketchPlane" : qUnion([Q0])});
            skLineSegment(sketch, "E83.bottom", {"start": v(20.5, -40.25) * mm, "end": v(12.5, -40.25) * mm, "construction": true});
            skLineSegment(sketch, "E83.top", {"start": v(20.5, -26.25) * mm, "end": v(12.5, -26.25) * mm});
            skLineSegment(sketch, "E83.left", {"start": v(20.5, -40.25) * mm, "end": v(20.5, -26.25) * mm});
            skLineSegment(sketch, "E83.right", {"start": v(12.5, -40.25) * mm, "end": v(12.5, -26.25) * mm});
            skLineSegment(sketch, "E84.bottom", {"start": v(-12.5, -40.25) * mm, "end": v(-20.5, -40.25) * mm, "construction": true});
            skLineSegment(sketch, "E84.top", {"start": v(-12.5, -26.25) * mm, "end": v(-20.5, -26.25) * mm});
            skLineSegment(sketch, "E84.left", {"start": v(-12.5, -40.25) * mm, "end": v(-12.5, -26.25) * mm});
            skLineSegment(sketch, "E84.right", {"start": v(-20.5, -40.25) * mm, "end": v(-20.5, -26.25) * mm});
            skLineSegment(sketch, "E85.bottom", {"start": v(20.5, 40.25) * mm, "end": v(12.5, 40.25) * mm, "construction": true});
            skLineSegment(sketch, "E85.top", {"start": v(20.5, 26.25) * mm, "end": v(12.5, 26.25) * mm});
            skLineSegment(sketch, "E85.left", {"start": v(20.5, 40.25) * mm, "end": v(20.5, 26.25) * mm});
            skLineSegment(sketch, "E85.right", {"start": v(12.5, 40.25) * mm, "end": v(12.5, 26.25) * mm});
            skLineSegment(sketch, "E86.bottom", {"start": v(-12.5, 40.25) * mm, "end": v(-20.5, 40.25) * mm, "construction": true});
            skLineSegment(sketch, "E86.top", {"start": v(-12.5, 26.25) * mm, "end": v(-20.5, 26.25) * mm});
            skLineSegment(sketch, "E86.left", {"start": v(-12.5, 40.25) * mm, "end": v(-12.5, 26.25) * mm});
            skLineSegment(sketch, "E86.right", {"start": v(-20.5, 40.25) * mm, "end": v(-20.5, 26.25) * mm});
            skLineSegment(sketch, "E87", {"start": v(12.5, -26.25) * mm, "end": v(-12.5, -26.25) * mm, "construction": true});
            skLineSegment(sketch, "E88", {"start": v(12.5, 26.25) * mm, "end": v(-12.5, 26.25) * mm, "construction": true});
            skLineSegment(sketch, "E89", {"start": v(0, 26.25) * mm, "end": v(0, 0) * mm, "construction": true});
            skLineSegment(sketch, "E90", {"start": v(0, 0) * mm, "end": v(0, -26.25) * mm, "construction": true});
            skLineSegment(sketch, "E91", {"start": v(20.5, -40.25) * mm, "end": v(20.5, -41.25) * mm});
            skLineSegment(sketch, "E92", {"start": v(20.5, -41.25) * mm, "end": v(12.5, -40.25) * mm});
            skLineSegment(sketch, "E93", {"start": v(-20.5, -40.25) * mm, "end": v(-20.5, -41.25) * mm});
            skLineSegment(sketch, "E94", {"start": v(-20.5, -41.25) * mm, "end": v(-12.5, -40.25) * mm});
            skLineSegment(sketch, "E95", {"start": v(-20.5, 40.25) * mm, "end": v(-20.5, 41.25) * mm});
            skLineSegment(sketch, "E96", {"start": v(-20.5, 41.25) * mm, "end": v(-12.5, 40.25) * mm});
            skLineSegment(sketch, "E97", {"start": v(20.5, 40.25) * mm, "end": v(20.5, 41.25) * mm});
            skLineSegment(sketch, "E98", {"start": v(20.5, 41.25) * mm, "end": v(12.5, 40.25) * mm});
            skSolve(sketch);
        }
        {
            var Q0;
            Q0 = qSketchRegion(id + "F9", true);
            extrude(context, id + "F10", {"entities" : qUnion([Q0]), "operationType" : NewBodyOperationType.REMOVE, "oppositeDirection" : true, "depth" : 1.75 * mm, "offsetDistance" : 25 * mm});
        }
        {
            var Q0;
            Q0=makeQuery(id+"F10.boolean.opBoolean","COPY",FACE,{"derivedFrom":makeQuery(id+"F10.opExtrude","CAP_FACE",FACE,{"disambiguationData":[OSD([sQuery(id+"F9.wireOp",EDGE,"E83.top"),sQuery(id+"F9.wireOp",EDGE,"E83.left"),sQuery(id+"F9.wireOp",EDGE,"E83.right"),sQuery(id+"F9.wireOp",EDGE,"E91"),sQuery(id+"F9.wireOp",EDGE,"E92")])],"isStart":false})});
            var sketch = newSketch(context, id + "F11", { "sketchPlane" : qUnion([Q0])});
            skLineSegment(sketch, "E99.bottom", {"start": v(12.5, -41.25) * mm, "end": v(20.5, -41.25) * mm});
            skLineSegment(sketch, "E99.top", {"start": v(12.5, -29.75) * mm, "end": v(20.5, -29.75) * mm});
            skLineSegment(sketch, "E99.left", {"start": v(12.5, -41.25) * mm, "end": v(12.5, -29.75) * mm});
            skLineSegment(sketch, "E99.right", {"start": v(20.5, -41.25) * mm, "end": v(20.5, -29.75) * mm});
            skLineSegment(sketch, "E100.top", {"start": v(-12.5, -29.75) * mm, "end": v(-20.5, -29.75) * mm});
            skLineSegment(sketch, "E100.right", {"start": v(-20.5, -41.25) * mm, "end": v(-20.5, -29.75) * mm});
            skLineSegment(sketch, "E101.bottom", {"start": v(12.5, 41.25) * mm, "end": v(20.5, 41.25) * mm});
            skLineSegment(sketch, "E101.top", {"start": v(12.5, 29.75) * mm, "end": v(20.5, 29.75) * mm});
            skLineSegment(sketch, "E101.left", {"start": v(12.5, 41.25) * mm, "end": v(12.5, 29.75) * mm});
            skLineSegment(sketch, "E101.right", {"start": v(20.5, 41.25) * mm, "end": v(20.5, 29.75) * mm});
            skLineSegment(sketch, "E102.bottom", {"start": v(-12.5, 41.25) * mm, "end": v(-20.5, 41.25) * mm});
            skLineSegment(sketch, "E102.top", {"start": v(-12.5, 29.75) * mm, "end": v(-20.5, 29.75) * mm});
            skLineSegment(sketch, "E102.left", {"start": v(-12.5, 41.25) * mm, "end": v(-12.5, 29.75) * mm});
            skLineSegment(sketch, "E102.right", {"start": v(-20.5, 41.25) * mm, "end": v(-20.5, 29.75) * mm});
            skLineSegment(sketch, "E103", {"start": v(-12.5, -29.75) * mm, "end": v(-12.5, -41.25) * mm});
            skLineSegment(sketch, "E104", {"start": v(-12.5, -41.25) * mm, "end": v(-20.5, -41.25) * mm});
            skSolve(sketch);
        }
        {
            var Q0;
            Q0 = qSketchRegion(id + "F11", true);
            extrude(context, id + "F12", {"entities" : qUnion([Q0]), "operationType" : NewBodyOperationType.REMOVE, "oppositeDirection" : true, "depth" : 1 * mm, "offsetDistance" : 25 * mm});
        }
        {
            var Q0;
            Q0=makeQuery(id+"F12.boolean.opBoolean","COPY",FACE,{"derivedFrom":makeQuery(id+"F12.opExtrude","CAP_FACE",FACE,{"disambiguationData":[OSD([sQuery(id+"F11.wireOp",EDGE,"E99.bottom"),sQuery(id+"F11.wireOp",EDGE,"E99.top"),sQuery(id+"F11.wireOp",EDGE,"E99.left"),sQuery(id+"F11.wireOp",EDGE,"E99.right")])],"isStart":false})});
            var sketch = newSketch(context, id + "F13", { "sketchPlane" : qUnion([Q0])});
            skLineSegment(sketch, "E105.bottom", {"start": v(20.5, -33.25) * mm, "end": v(12.5, -33.25) * mm});
            skLineSegment(sketch, "E105.top", {"start": v(20.5, -41.25) * mm, "end": v(12.5, -41.25) * mm});
            skLineSegment(sketch, "E105.left", {"start": v(20.5, -33.25) * mm, "end": v(20.5, -41.25) * mm});
            skLineSegment(sketch, "E105.right", {"start": v(12.5, -33.25) * mm, "end": v(12.5, -41.25) * mm});
            skLineSegment(sketch, "E106.bottom", {"start": v(-12.5, -33.25) * mm, "end": v(-20.5, -33.25) * mm});
            skLineSegment(sketch, "E106.top", {"start": v(-12.5, -41.25) * mm, "end": v(-20.5, -41.25) * mm});
            skLineSegment(sketch, "E106.left", {"start": v(-12.5, -33.25) * mm, "end": v(-12.5, -41.25) * mm});
            skLineSegment(sketch, "E106.right", {"start": v(-20.5, -33.25) * mm, "end": v(-20.5, -41.25) * mm});
            skLineSegment(sketch, "E107.bottom", {"start": v(20.5, 33.25) * mm, "end": v(12.5, 33.25) * mm});
            skLineSegment(sketch, "E107.top", {"start": v(20.5, 41.25) * mm, "end": v(12.5, 41.25) * mm});
            skLineSegment(sketch, "E107.left", {"start": v(20.5, 33.25) * mm, "end": v(20.5, 41.25) * mm});
            skLineSegment(sketch, "E107.right", {"start": v(12.5, 33.25) * mm, "end": v(12.5, 41.25) * mm});
            skLineSegment(sketch, "E108.bottom", {"start": v(-12.5, 33.25) * mm, "end": v(-20.5, 33.25) * mm});
            skLineSegment(sketch, "E108.top", {"start": v(-12.5, 41.25) * mm, "end": v(-20.5, 41.25) * mm});
            skLineSegment(sketch, "E108.left", {"start": v(-12.5, 33.25) * mm, "end": v(-12.5, 41.25) * mm});
            skLineSegment(sketch, "E108.right", {"start": v(-20.5, 33.25) * mm, "end": v(-20.5, 41.25) * mm});
            skSolve(sketch);
        }
        {
            var Q0;
            Q0 = qSketchRegion(id + "F13", true);
            extrude(context, id + "F14", {"entities" : qUnion([Q0]), "operationType" : NewBodyOperationType.REMOVE, "oppositeDirection" : true, "depth" : 1 * mm, "offsetDistance" : 25 * mm});
        }
        {
            var Q0;
            Q0=makeQuery(id+"F14.boolean.opBoolean","COPY",FACE,{"derivedFrom":makeQuery(id+"F14.opExtrude","CAP_FACE",FACE,{"disambiguationData":[OSD([sQuery(id+"F13.wireOp",EDGE,"E105.bottom"),sQuery(id+"F13.wireOp",EDGE,"E105.top"),sQuery(id+"F13.wireOp",EDGE,"E105.left"),sQuery(id+"F13.wireOp",EDGE,"E105.right")])],"isStart":false})});
            var sketch = newSketch(context, id + "F15", { "sketchPlane" : qUnion([Q0])});
            skLineSegment(sketch, "E109.bottom", {"start": v(20.5, -41.25) * mm, "end": v(12.5, -41.25) * mm});
            skLineSegment(sketch, "E109.top", {"start": v(20.5, -36.75) * mm, "end": v(12.5, -36.75) * mm});
            skLineSegment(sketch, "E109.left", {"start": v(20.5, -41.25) * mm, "end": v(20.5, -36.75) * mm});
            skLineSegment(sketch, "E109.right", {"start": v(12.5, -41.25) * mm, "end": v(12.5, -36.75) * mm});
            skLineSegment(sketch, "E110.bottom", {"start": v(-12.5, -41.25) * mm, "end": v(-20.5, -41.25) * mm});
            skLineSegment(sketch, "E110.top", {"start": v(-12.5, -36.75) * mm, "end": v(-20.5, -36.75) * mm});
            skLineSegment(sketch, "E110.left", {"start": v(-12.5, -41.25) * mm, "end": v(-12.5, -36.75) * mm});
            skLineSegment(sketch, "E110.right", {"start": v(-20.5, -41.25) * mm, "end": v(-20.5, -36.75) * mm});
            skLineSegment(sketch, "E111.bottom", {"start": v(20.5, 36.75) * mm, "end": v(12.5, 36.75) * mm});
            skLineSegment(sketch, "E111.top", {"start": v(20.5, 41.25) * mm, "end": v(12.5, 41.25) * mm});
            skLineSegment(sketch, "E111.left", {"start": v(20.5, 36.75) * mm, "end": v(20.5, 41.25) * mm});
            skLineSegment(sketch, "E111.right", {"start": v(12.5, 36.75) * mm, "end": v(12.5, 41.25) * mm});
            skLineSegment(sketch, "E112.bottom", {"start": v(-12.5, 36.75) * mm, "end": v(-20.5, 36.75) * mm});
            skLineSegment(sketch, "E112.top", {"start": v(-12.5, 41.25) * mm, "end": v(-20.5, 41.25) * mm});
            skLineSegment(sketch, "E112.left", {"start": v(-12.5, 36.75) * mm, "end": v(-12.5, 41.25) * mm});
            skLineSegment(sketch, "E112.right", {"start": v(-20.5, 36.75) * mm, "end": v(-20.5, 41.25) * mm});
            skSolve(sketch);
        }
        {
            var Q0;
            Q0 = qSketchRegion(id + "F15", true);
            extrude(context, id + "F16", {"entities" : qUnion([Q0]), "operationType" : NewBodyOperationType.REMOVE, "oppositeDirection" : true, "depth" : 1 * mm, "offsetDistance" : 25 * mm});
        }
        {
            var Q0;
            Q0=makeQuery(id+"F8.boolean.opBoolean","COPY",EDGE,{"derivedFrom":makeQuery(id+"F8.opExtrude","SWEPT_EDGE",EDGE,{"disambiguationData":[OSD([sQuery(id+"F7.wireOp",EDGE,"E71.right"),sQuery(id+"F7.wireOp",EDGE,"E72")])]})});
            var Q1;
            Q1=makeQuery(id+"F8.boolean.opBoolean","COPY",EDGE,{"derivedFrom":makeQuery(id+"F8.opExtrude","SWEPT_EDGE",EDGE,{"disambiguationData":[OSD([sQuery(id+"F7.wireOp",EDGE,"E75"),sQuery(id+"F7.wireOp",EDGE,"E76")])]})});
            var Q2;
            Q2=makeQuery(id+"F8.boolean.opBoolean","COPY",EDGE,{"derivedFrom":makeQuery(id+"F8.opExtrude","SWEPT_EDGE",EDGE,{"disambiguationData":[OSD([sQuery(id+"F7.wireOp",EDGE,"E71.left"),sQuery(id+"F7.wireOp",EDGE,"E76")])]})});
            var Q3;
            Q3=makeQuery(id+"F8.boolean.opBoolean","COPY",EDGE,{"derivedFrom":makeQuery(id+"F8.opExtrude","SWEPT_EDGE",EDGE,{"disambiguationData":[OSD([sQuery(id+"F7.wireOp",EDGE,"E72"),sQuery(id+"F7.wireOp",EDGE,"E73")])]})});
            var Q4;
            Q4=makeQuery(id+"F8.boolean.opBoolean","COPY",EDGE,{"derivedFrom":makeQuery(id+"F8.opExtrude","SWEPT_EDGE",EDGE,{"disambiguationData":[OSD([sQuery(id+"F7.wireOp",EDGE,"E80"),sQuery(id+"F7.wireOp",EDGE,"E81")])]})});
            var Q5;
            Q5=makeQuery(id+"F8.boolean.opBoolean","COPY",EDGE,{"derivedFrom":makeQuery(id+"F8.opExtrude","SWEPT_EDGE",EDGE,{"disambiguationData":[OSD([sQuery(id+"F7.wireOp",EDGE,"E71.right"),sQuery(id+"F7.wireOp",EDGE,"E77")])]})});
            var Q6;
            Q6=makeQuery(id+"F8.boolean.opBoolean","COPY",EDGE,{"derivedFrom":makeQuery(id+"F8.opExtrude","SWEPT_EDGE",EDGE,{"disambiguationData":[OSD([sQuery(id+"F7.wireOp",EDGE,"E77"),sQuery(id+"F7.wireOp",EDGE,"E78")])]})});
            var Q7;
            Q7=makeQuery(id+"F8.boolean.opBoolean","COPY",EDGE,{"derivedFrom":makeQuery(id+"F8.opExtrude","SWEPT_EDGE",EDGE,{"disambiguationData":[OSD([sQuery(id+"F7.wireOp",EDGE,"E71.left"),sQuery(id+"F7.wireOp",EDGE,"E81")])]})});
            var Q8;
            Q8=makeQuery(id+"F8.boolean.opBoolean","COPY",EDGE,{"derivedFrom":makeQuery(id+"F8.opExtrude","SWEPT_EDGE",EDGE,{"disambiguationData":[OSD([sQuery(id+"F7.wireOp",EDGE,"E82.1.0.7"),sQuery(id+"F7.wireOp",EDGE,"E82.1.0.12")])]})});
            var Q9;
            Q9=makeQuery(id+"F8.boolean.opBoolean","COPY",EDGE,{"derivedFrom":makeQuery(id+"F8.opExtrude","SWEPT_EDGE",EDGE,{"disambiguationData":[OSD([sQuery(id+"F7.wireOp",EDGE,"E82.1.0.8"),sQuery(id+"F7.wireOp",EDGE,"E82.1.0.15")])]})});
            var Q10;
            Q10=makeQuery(id+"F8.boolean.opBoolean","COPY",EDGE,{"derivedFrom":makeQuery(id+"F8.opExtrude","SWEPT_EDGE",EDGE,{"disambiguationData":[OSD([sQuery(id+"F7.wireOp",EDGE,"E82.1.0.9"),sQuery(id+"F7.wireOp",EDGE,"E82.1.0.12")])]})});
            var Q11;
            Q11=makeQuery(id+"F8.boolean.opBoolean","COPY",EDGE,{"derivedFrom":makeQuery(id+"F8.opExtrude","SWEPT_EDGE",EDGE,{"disambiguationData":[OSD([sQuery(id+"F7.wireOp",EDGE,"E82.1.0.5"),sQuery(id+"F7.wireOp",EDGE,"E82.1.0.15")])]})});
            var Q12;
            Q12=makeQuery(id+"F8.boolean.opBoolean","COPY",EDGE,{"derivedFrom":makeQuery(id+"F8.opExtrude","SWEPT_EDGE",EDGE,{"disambiguationData":[OSD([sQuery(id+"F7.wireOp",EDGE,"E82.1.0.11"),sQuery(id+"F7.wireOp",EDGE,"E82.1.0.13")])]})});
            var Q13;
            Q13=makeQuery(id+"F8.boolean.opBoolean","COPY",EDGE,{"derivedFrom":makeQuery(id+"F8.opExtrude","SWEPT_EDGE",EDGE,{"disambiguationData":[OSD([sQuery(id+"F7.wireOp",EDGE,"E82.1.0.7"),sQuery(id+"F7.wireOp",EDGE,"E82.1.0.10")])]})});
            var Q14;
            Q14=makeQuery(id+"F8.boolean.opBoolean","COPY",EDGE,{"derivedFrom":makeQuery(id+"F8.opExtrude","SWEPT_EDGE",EDGE,{"disambiguationData":[OSD([sQuery(id+"F7.wireOp",EDGE,"E82.1.0.5"),sQuery(id+"F7.wireOp",EDGE,"E82.1.0.11")])]})});
            var Q15;
            Q15=makeQuery(id+"F8.boolean.opBoolean","COPY",EDGE,{"derivedFrom":makeQuery(id+"F8.opExtrude","SWEPT_EDGE",EDGE,{"disambiguationData":[OSD([sQuery(id+"F7.wireOp",EDGE,"E82.1.0.10"),sQuery(id+"F7.wireOp",EDGE,"E82.1.0.14")])]})});
            var Q16;
            Q16=makeQuery(id+"F8.boolean.opBoolean","COPY",EDGE,{"derivedFrom":makeQuery(id+"F8.opExtrude","SWEPT_EDGE",EDGE,{"disambiguationData":[OSD([sQuery(id+"F7.wireOp",EDGE,"E82.1.1.5"),sQuery(id+"F7.wireOp",EDGE,"E82.1.1.11")])]})});
            var Q17;
            Q17=makeQuery(id+"F8.boolean.opBoolean","COPY",EDGE,{"derivedFrom":makeQuery(id+"F8.opExtrude","SWEPT_EDGE",EDGE,{"disambiguationData":[OSD([sQuery(id+"F7.wireOp",EDGE,"E82.1.1.10"),sQuery(id+"F7.wireOp",EDGE,"E82.1.1.14")])]})});
            var Q18;
            Q18=makeQuery(id+"F8.boolean.opBoolean","COPY",EDGE,{"derivedFrom":makeQuery(id+"F8.opExtrude","SWEPT_EDGE",EDGE,{"disambiguationData":[OSD([sQuery(id+"F7.wireOp",EDGE,"E82.1.1.11"),sQuery(id+"F7.wireOp",EDGE,"E82.1.1.13")])]})});
            var Q19;
            Q19=makeQuery(id+"F8.boolean.opBoolean","COPY",EDGE,{"derivedFrom":makeQuery(id+"F8.opExtrude","SWEPT_EDGE",EDGE,{"disambiguationData":[OSD([sQuery(id+"F7.wireOp",EDGE,"E82.1.1.7"),sQuery(id+"F7.wireOp",EDGE,"E82.1.1.10")])]})});
            var Q20;
            Q20=makeQuery(id+"F8.boolean.opBoolean","COPY",EDGE,{"derivedFrom":makeQuery(id+"F8.opExtrude","SWEPT_EDGE",EDGE,{"disambiguationData":[OSD([sQuery(id+"F7.wireOp",EDGE,"E82.1.1.7"),sQuery(id+"F7.wireOp",EDGE,"E82.1.1.12")])]})});
            var Q21;
            Q21=makeQuery(id+"F8.boolean.opBoolean","COPY",EDGE,{"derivedFrom":makeQuery(id+"F8.opExtrude","SWEPT_EDGE",EDGE,{"disambiguationData":[OSD([sQuery(id+"F7.wireOp",EDGE,"E82.1.1.8"),sQuery(id+"F7.wireOp",EDGE,"E82.1.1.15")])]})});
            var Q22;
            Q22=makeQuery(id+"F8.boolean.opBoolean","COPY",EDGE,{"derivedFrom":makeQuery(id+"F8.opExtrude","SWEPT_EDGE",EDGE,{"disambiguationData":[OSD([sQuery(id+"F7.wireOp",EDGE,"E82.1.1.9"),sQuery(id+"F7.wireOp",EDGE,"E82.1.1.12")])]})});
            var Q23;
            Q23=makeQuery(id+"F8.boolean.opBoolean","COPY",EDGE,{"derivedFrom":makeQuery(id+"F8.opExtrude","SWEPT_EDGE",EDGE,{"disambiguationData":[OSD([sQuery(id+"F7.wireOp",EDGE,"E82.1.1.5"),sQuery(id+"F7.wireOp",EDGE,"E82.1.1.15")])]})});
            var Q24;
            Q24=makeQuery(id+"F8.boolean.opBoolean","COPY",EDGE,{"derivedFrom":makeQuery(id+"F8.opExtrude","SWEPT_EDGE",EDGE,{"disambiguationData":[OSD([sQuery(id+"F7.wireOp",EDGE,"E82.0.1.9"),sQuery(id+"F7.wireOp",EDGE,"E82.0.1.12")])]})});
            var Q25;
            Q25=makeQuery(id+"F8.boolean.opBoolean","COPY",EDGE,{"derivedFrom":makeQuery(id+"F8.opExtrude","SWEPT_EDGE",EDGE,{"disambiguationData":[OSD([sQuery(id+"F7.wireOp",EDGE,"E82.0.1.5"),sQuery(id+"F7.wireOp",EDGE,"E82.0.1.15")])]})});
            var Q26;
            Q26=makeQuery(id+"F8.boolean.opBoolean","COPY",EDGE,{"derivedFrom":makeQuery(id+"F8.opExtrude","SWEPT_EDGE",EDGE,{"disambiguationData":[OSD([sQuery(id+"F7.wireOp",EDGE,"E82.0.1.7"),sQuery(id+"F7.wireOp",EDGE,"E82.0.1.12")])]})});
            var Q27;
            Q27=makeQuery(id+"F8.boolean.opBoolean","COPY",EDGE,{"derivedFrom":makeQuery(id+"F8.opExtrude","SWEPT_EDGE",EDGE,{"disambiguationData":[OSD([sQuery(id+"F7.wireOp",EDGE,"E82.0.1.8"),sQuery(id+"F7.wireOp",EDGE,"E82.0.1.15")])]})});
            var Q28;
            Q28=makeQuery(id+"F8.boolean.opBoolean","COPY",EDGE,{"derivedFrom":makeQuery(id+"F8.opExtrude","SWEPT_EDGE",EDGE,{"disambiguationData":[OSD([sQuery(id+"F7.wireOp",EDGE,"E82.0.1.11"),sQuery(id+"F7.wireOp",EDGE,"E82.0.1.13")])]})});
            var Q29;
            Q29=makeQuery(id+"F8.boolean.opBoolean","COPY",EDGE,{"derivedFrom":makeQuery(id+"F8.opExtrude","SWEPT_EDGE",EDGE,{"disambiguationData":[OSD([sQuery(id+"F7.wireOp",EDGE,"E82.0.1.7"),sQuery(id+"F7.wireOp",EDGE,"E82.0.1.10")])]})});
            var Q30;
            Q30=makeQuery(id+"F8.boolean.opBoolean","COPY",EDGE,{"derivedFrom":makeQuery(id+"F8.opExtrude","SWEPT_EDGE",EDGE,{"disambiguationData":[OSD([sQuery(id+"F7.wireOp",EDGE,"E82.0.1.10"),sQuery(id+"F7.wireOp",EDGE,"E82.0.1.14")])]})});
            var Q31;
            Q31=makeQuery(id+"F8.boolean.opBoolean","COPY",EDGE,{"derivedFrom":makeQuery(id+"F8.opExtrude","SWEPT_EDGE",EDGE,{"disambiguationData":[OSD([sQuery(id+"F7.wireOp",EDGE,"E82.0.1.5"),sQuery(id+"F7.wireOp",EDGE,"E82.0.1.11")])]})});
            fillet(context, id + "F17", {"entities" : qUnion([Q0, Q1, Q2, Q3, Q4, Q5, Q6, Q7, Q8, Q9, Q10, Q11, Q12, Q13, Q14, Q15, Q16, Q17, Q18, Q19, Q20, Q21, Q22, Q23, Q24, Q25, Q26, Q27, Q28, Q29, Q30, Q31]), "radius" : 1 * mm, "tangentPropagation" : true, "allowEdgeOverflow" : false});
        }
    });
